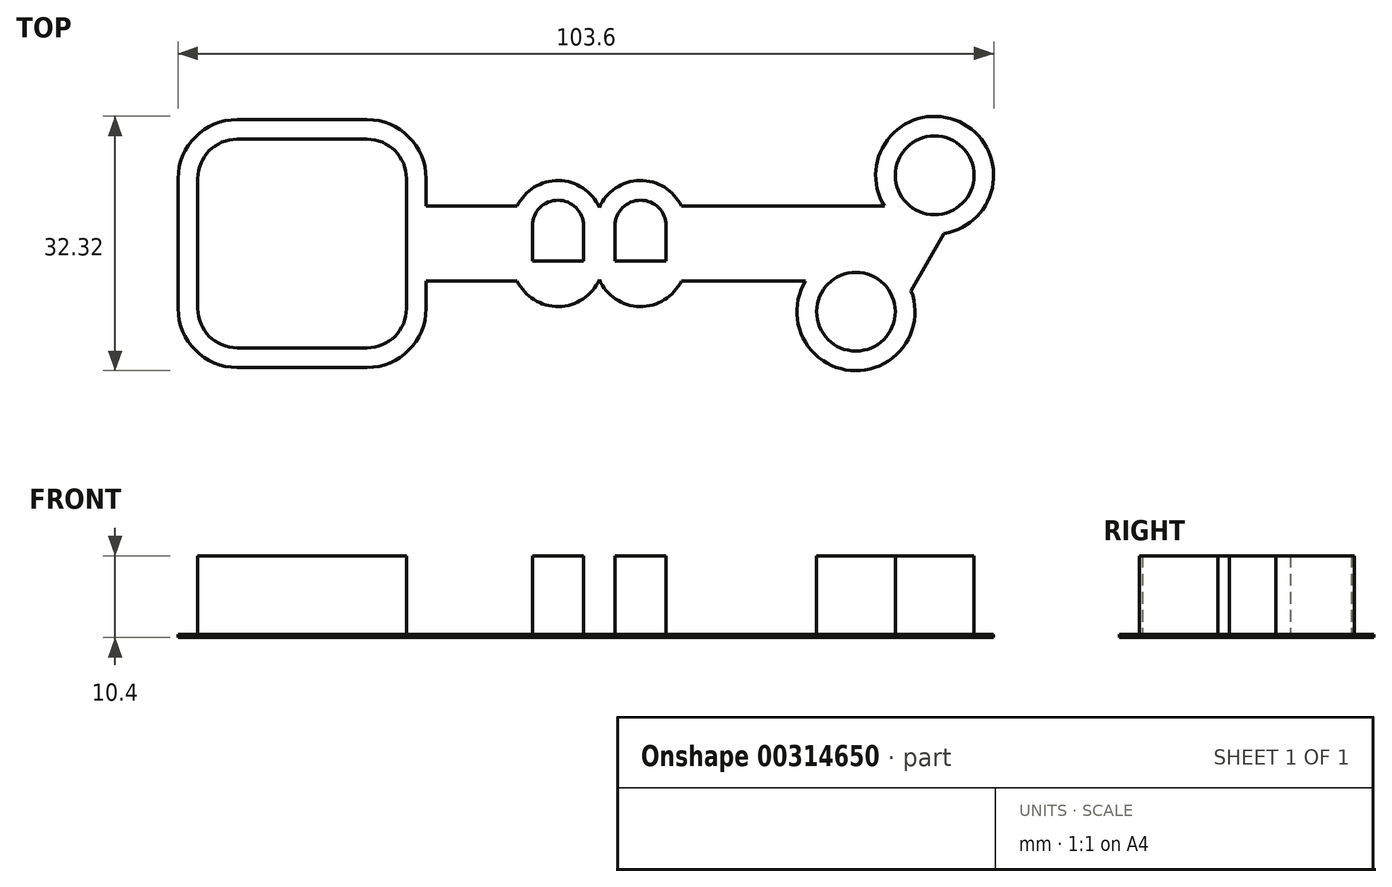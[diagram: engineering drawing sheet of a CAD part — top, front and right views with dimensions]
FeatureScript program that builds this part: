
annotation { "Feature Type Name" : "Feature", "Feature Type Description" : "" }
export const myFeature = defineFeature(function(context is Context, id is Id, definition is map)
    precondition{}
    {
        {
            var Q0;
            Q0=qCreatedBy(makeId("Top.planeOp"),FACE);
            var sketch = newSketch(context, id + "F0", { "sketchPlane" : qUnion([Q0])});
            skLineSegment(sketch, "E0.bottom", {"start": v(8.25, 13.25) * mm, "end": v(-8.25, 13.25) * mm});
            skLineSegment(sketch, "E0.top", {"start": v(8.25, -13.25) * mm, "end": v(-8.25, -13.25) * mm});
            skLineSegment(sketch, "E0.left", {"start": v(13.25, 8.25) * mm, "end": v(13.25, 2.25) * mm});
            skLineSegment(sketch, "E0.right", {"start": v(-13.25, 8.25) * mm, "end": v(-13.25, -8.25) * mm});
            skPoint(sketch, "E0.middle", {"position": v(0, 0) * mm});
            skPoint(sketch, "E1.visualSharp", {"position": v(-13.25, 13.25) * mm});
            skArc(sketch, "E1.filletArc", {"start": v(-8.25, 13.25) * mm, "mid": v(-11.79, 11.79) * mm, "end": v(-13.25, 8.25) * mm});
            skPoint(sketch, "E2.visualSharp", {"position": v(13.25, 13.25) * mm});
            skArc(sketch, "E2.filletArc", {"start": v(13.25, 8.25) * mm, "mid": v(11.79, 11.79) * mm, "end": v(8.25, 13.25) * mm});
            skPoint(sketch, "E3.visualSharp", {"position": v(13.25, -13.25) * mm});
            skArc(sketch, "E3.filletArc", {"start": v(8.25, -13.25) * mm, "mid": v(11.79, -11.79) * mm, "end": v(13.25, -8.25) * mm});
            skPoint(sketch, "E4.visualSharp", {"position": v(-13.25, -13.25) * mm});
            skArc(sketch, "E4.filletArc", {"start": v(-13.25, -8.25) * mm, "mid": v(-11.79, -11.79) * mm, "end": v(-8.25, -13.25) * mm});
            skCircle(sketch, "E5", {"center": v(0, 0) * mm, "radius": 4.5 * mm});
            skLineSegment(sketch, "E6", {"start": v(-4.5, 13.25) * mm, "end": v(-4.5, -13.25) * mm});
            skLineSegment(sketch, "E7", {"start": v(4.5, 13.25) * mm, "end": v(4.5, -13.25) * mm});
            skLineSegment(sketch, "E8", {"start": v(-13.25, 4.5) * mm, "end": v(13.25, 4.5) * mm});
            skLineSegment(sketch, "E9", {"start": v(-13.25, -4.5) * mm, "end": v(13.25, -4.5) * mm});
            skLineSegment(sketch, "E10", {"start": v(-129.37, 0) * mm, "end": v(144.98, 0) * mm, "construction": true});
            skPoint(sketch, "E10.startSnap0", {"position": v(-13.25, 0) * mm});
            skPoint(sketch, "E10.endSnap0", {"position": v(13.25, 0) * mm});
            skLineSegment(sketch, "E11", {"start": v(13.25, 2.25) * mm, "end": v(13.25, 2.25) * mm});
            skLineSegment(sketch, "E12.MirrorCS", {"start": v(13.25, -2.25) * mm, "end": v(29.25, -2.25) * mm});
            skLineSegment(sketch, "E13.bottom", {"start": v(29.25, 2.25) * mm, "end": v(35.75, 2.25) * mm});
            skLineSegment(sketch, "E13.top", {"start": v(29.25, -2.25) * mm, "end": v(35.75, -2.25) * mm});
            skLineSegment(sketch, "E13.left", {"start": v(29.25, 2.25) * mm, "end": v(29.25, -2.25) * mm});
            skLineSegment(sketch, "E13.right", {"start": v(35.75, 2.25) * mm, "end": v(35.75, -2.25) * mm});
            skLineSegment(sketch, "E14", {"start": v(37.75, 27.76) * mm, "end": v(37.75, -22.07) * mm, "construction": true});
            skLineSegment(sketch, "E15.MirrorCS", {"start": v(39.75, 2.25) * mm, "end": v(39.75, -2.25) * mm});
            skLineSegment(sketch, "E16.MirrorCS", {"start": v(46.25, -2.25) * mm, "end": v(39.75, -2.25) * mm});
            skLineSegment(sketch, "E17.MirrorCS", {"start": v(46.25, 2.25) * mm, "end": v(39.75, 2.25) * mm});
            skLineSegment(sketch, "E18.MirrorCS", {"start": v(46.25, 2.25) * mm, "end": v(46.25, -2.25) * mm});
            skLineSegment(sketch, "E19", {"start": v(35.75, 2.25) * mm, "end": v(39.75, 2.25) * mm});
            skLineSegment(sketch, "E20", {"start": v(35.75, -2.25) * mm, "end": v(39.75, -2.25) * mm});
            skArc(sketch, "E21", {"start": v(29.25, 2.25) * mm, "mid": v(32.5, 5.5) * mm, "end": v(35.75, 2.25) * mm});
            skArc(sketch, "E22.MirrorCS", {"start": v(46.25, 2.25) * mm, "mid": v(43, 5.5) * mm, "end": v(39.75, 2.25) * mm});
            skArc(sketch, "E23.MirrorCS", {"start": v(46.25, -2.25) * mm, "mid": v(43, -5.5) * mm, "end": v(39.75, -2.25) * mm});
            skArc(sketch, "E24.MirrorCS", {"start": v(29.25, -2.25) * mm, "mid": v(32.5, -5.5) * mm, "end": v(35.75, -2.25) * mm});
            skLineSegment(sketch, "E25", {"start": v(80.35, 8.66) * mm, "end": v(70.35, -8.66) * mm, "construction": true});
            skPoint(sketch, "E26", {"position": v(75.35, 0) * mm});
            skLineSegment(sketch, "E27", {"start": v(76.17, 5.92) * mm, "end": v(74.05, 2.25) * mm});
            skLineSegment(sketch, "E28.MirrorCS", {"start": v(80.06, 3.67) * mm, "end": v(74.53, -5.92) * mm});
            skPoint(sketch, "E29", {"position": v(72.75, 0) * mm});
            skLineSegment(sketch, "E30", {"start": v(46.25, 2.25) * mm, "end": v(74.05, 2.25) * mm});
            skLineSegment(sketch, "E31.MirrorCS", {"start": v(46.25, -2.25) * mm, "end": v(71.45, -2.25) * mm});
            skLineSegment(sketch, "E32", {"start": v(13.25, 2.25) * mm, "end": v(29.25, 2.25) * mm});
            skLineSegment(sketch, "E33", {"start": v(13.25, -2.25) * mm, "end": v(13.25, -8.25) * mm});
            skLineSegment(sketch, "E34", {"start": v(74.05, 2.25) * mm, "end": v(71.45, -2.25) * mm});
            skLineSegment(sketch, "E35", {"start": v(71.45, -2.25) * mm, "end": v(71.45, -2.25) * mm});
            skArc(sketch, "E36", {"start": v(70.63, -3.67) * mm, "mid": v(67.85, -13) * mm, "end": v(74.53, -5.92) * mm});
            skArc(sketch, "E37", {"start": v(74.53, -5.92) * mm, "mid": v(72.85, -4.33) * mm, "end": v(70.63, -3.67) * mm});
            skArc(sketch, "E38", {"start": v(76.17, 5.92) * mm, "mid": v(77.85, 4.33) * mm, "end": v(80.06, 3.67) * mm});
            skArc(sketch, "E39", {"start": v(80.06, 3.67) * mm, "mid": v(82.85, 13) * mm, "end": v(76.17, 5.92) * mm});
            skLineSegment(sketch, "E40", {"start": v(71.45, -2.25) * mm, "end": v(70.63, -3.67) * mm});
            skLineSegment(sketch, "E41", {"start": v(13.25, 2.25) * mm, "end": v(13.25, -2.25) * mm});
            skLineSegment(sketch, "E42.0", {"start": v(15.75, 8.25) * mm, "end": v(15.75, 4.75) * mm});
            skArc(sketch, "E42.1", {"start": v(15.75, 8.25) * mm, "mid": v(13.55, 13.55) * mm, "end": v(8.25, 15.75) * mm});
            skLineSegment(sketch, "E42.2", {"start": v(8.25, 15.75) * mm, "end": v(-8.25, 15.75) * mm});
            skArc(sketch, "E42.3", {"start": v(-8.25, 15.75) * mm, "mid": v(-13.55, 13.55) * mm, "end": v(-15.75, 8.25) * mm});
            skLineSegment(sketch, "E42.4", {"start": v(-15.75, 8.25) * mm, "end": v(-15.75, -8.25) * mm});
            skLineSegment(sketch, "E42.5", {"start": v(15.75, 4.75) * mm, "end": v(27.32, 4.75) * mm});
            skArc(sketch, "E42.6", {"start": v(-15.75, -8.25) * mm, "mid": v(-13.55, -13.55) * mm, "end": v(-8.25, -15.75) * mm});
            skLineSegment(sketch, "E42.7", {"start": v(8.25, -15.75) * mm, "end": v(-8.25, -15.75) * mm});
            skArc(sketch, "E42.8", {"start": v(8.25, -15.75) * mm, "mid": v(13.55, -13.55) * mm, "end": v(15.75, -8.25) * mm});
            skLineSegment(sketch, "E42.9", {"start": v(15.75, -4.75) * mm, "end": v(15.75, -8.25) * mm});
            skArc(sketch, "E42.10", {"start": v(81.56, 1.26) * mm, "mid": v(83.47, 15.48) * mm, "end": v(73.95, 4.75) * mm});
            skLineSegment(sketch, "E42.11", {"start": v(48.18, 4.75) * mm, "end": v(73.95, 4.75) * mm});
            skArc(sketch, "E42.12", {"start": v(48.18, 4.75) * mm, "mid": v(42.91, 8) * mm, "end": v(37.75, 4.6) * mm});
            skArc(sketch, "E42.13", {"start": v(27.32, 4.75) * mm, "mid": v(32.59, 8) * mm, "end": v(37.75, 4.6) * mm});
            skLineSegment(sketch, "E42.14", {"start": v(81.56, 1.26) * mm, "end": v(77.36, -6) * mm});
            skArc(sketch, "E42.15", {"start": v(63.95, -4.75) * mm, "mid": v(69.65, -16.13) * mm, "end": v(77.36, -6) * mm});
            skLineSegment(sketch, "E42.16", {"start": v(48.18, -4.75) * mm, "end": v(63.95, -4.75) * mm});
            skArc(sketch, "E42.17", {"start": v(48.18, -4.75) * mm, "mid": v(42.91, -8) * mm, "end": v(37.75, -4.6) * mm});
            skArc(sketch, "E42.18", {"start": v(27.32, -4.75) * mm, "mid": v(32.59, -8) * mm, "end": v(37.75, -4.6) * mm});
            skLineSegment(sketch, "E42.19", {"start": v(15.75, -4.75) * mm, "end": v(27.32, -4.75) * mm});
            skSolve(sketch);
        }
        {
            var Q0;
            {var subQ10=sQuery(id+"F0.wireOp",EDGE,"E1.filletArc");Q0=makeQuery(id+"F0.imprint","IMPRINT",FACE,{"disambiguationData":[TD([[makeQuery(id+"F0.imprint","IMPRINT",EDGE,{"derivedFrom":subQ10}),-1.0]])]});}
            var Q1;
            Q1=makeQuery(id+"F0.imprint","IMPRINT",FACE,{"disambiguationData":[TD([[makeQuery(id+"F0.imprint","IMPRINT",EDGE,{"derivedFrom":sQuery(id+"F0.wireOp",EDGE,"E13.right")}),1.0]])]});
            var Q2;
            {var subQ0=sQuery(id+"F0.wireOp",EDGE,"E8");var subQ1=sQuery(id+"F0.wireOp",EDGE,"E5");var subQ2=makeQuery(id+"F0.imprint","INTERSECT",VERTEX,{"derivedFrom":[subQ1,subQ0]});Q2=makeQuery(id+"F0.imprint","IMPRINT",FACE,{"disambiguationData":[TD([[makeQuery(id+"F0.imprint","IMPRINT",EDGE,{"disambiguationData":[TD([[subQ2,1.0]])],"derivedFrom":subQ1}),-1.0]])]});}
            var Q3;
            Q3=makeQuery(id+"F0.imprint","IMPRINT",FACE,{"disambiguationData":[TD([[makeQuery(id+"F0.imprint","IMPRINT",EDGE,{"derivedFrom":sQuery(id+"F0.wireOp",EDGE,"E12.MirrorCS")}),1.0]])]});
            var Q4;
            Q4=makeQuery(id+"F0.imprint","IMPRINT",FACE,{"disambiguationData":[TD([[makeQuery(id+"F0.imprint","IMPRINT",EDGE,{"derivedFrom":sQuery(id+"F0.wireOp",EDGE,"E18.MirrorCS")}),1.0]])]});
            var Q5;
            {var subQ5=sQuery(id+"F0.wireOp",EDGE,"E2.filletArc");Q5=makeQuery(id+"F0.imprint","IMPRINT",FACE,{"disambiguationData":[TD([[makeQuery(id+"F0.imprint","IMPRINT",EDGE,{"derivedFrom":subQ5}),1.0]])]});}
            var Q6;
            {var subQ2=sQuery(id+"F0.wireOp",EDGE,"E6");var subQ5=sQuery(id+"F0.wireOp",EDGE,"E0.bottom");var subQ8=makeQuery(id+"F0.imprint","INTERSECT",VERTEX,{"derivedFrom":[subQ5,subQ2]});Q6=makeQuery(id+"F0.imprint","IMPRINT",FACE,{"disambiguationData":[TD([[makeQuery(id+"F0.imprint","IMPRINT",EDGE,{"disambiguationData":[TD([[subQ8,1.0]])],"derivedFrom":subQ5}),1.0]])]});}
            var Q7;
            {var subQ0=sQuery(id+"F0.wireOp",EDGE,"E8");var subQ1=sQuery(id+"F0.wireOp",EDGE,"E5");var subQ2=makeQuery(id+"F0.imprint","INTERSECT",VERTEX,{"derivedFrom":[subQ1,subQ0]});Q7=makeQuery(id+"F0.imprint","IMPRINT",FACE,{"disambiguationData":[TD([[makeQuery(id+"F0.imprint","IMPRINT",EDGE,{"disambiguationData":[TD([[subQ2,-1.0]])],"derivedFrom":subQ1}),-1.0]])]});}
            var Q8;
            {var subQ5=sQuery(id+"F0.wireOp",EDGE,"E1.filletArc");Q8=makeQuery(id+"F0.imprint","IMPRINT",FACE,{"disambiguationData":[TD([[makeQuery(id+"F0.imprint","IMPRINT",EDGE,{"derivedFrom":subQ5}),1.0]])]});}
            var Q9;
            {var subQ0=sQuery(id+"F0.wireOp",EDGE,"E6");var subQ1=sQuery(id+"F0.wireOp",EDGE,"E5");var subQ2=makeQuery(id+"F0.imprint","INTERSECT",VERTEX,{"derivedFrom":[subQ1,subQ0]});Q9=makeQuery(id+"F0.imprint","IMPRINT",FACE,{"disambiguationData":[TD([[makeQuery(id+"F0.imprint","IMPRINT",EDGE,{"disambiguationData":[TD([[subQ2,-1.0]])],"derivedFrom":subQ1}),-1.0]])]});}
            var Q10;
            {var subQ0=sQuery(id+"F0.wireOp",EDGE,"E8");var subQ1=sQuery(id+"F0.wireOp",EDGE,"E0.right");var subQ2=makeQuery(id+"F0.imprint","INTERSECT",VERTEX,{"derivedFrom":[subQ1,subQ0]});Q10=makeQuery(id+"F0.imprint","IMPRINT",FACE,{"disambiguationData":[TD([[makeQuery(id+"F0.imprint","IMPRINT",EDGE,{"disambiguationData":[TD([[subQ2,-1.0]])],"derivedFrom":subQ1}),1.0]])]});}
            var Q11;
            Q11=makeQuery(id+"F0.imprint","IMPRINT",FACE,{"disambiguationData":[TD([[makeQuery(id+"F0.imprint","IMPRINT",EDGE,{"derivedFrom":sQuery(id+"F0.wireOp",EDGE,"E27")}),1.0]])]});
            var Q12;
            {var subQ5=sQuery(id+"F0.wireOp",EDGE,"E3.filletArc");Q12=makeQuery(id+"F0.imprint","IMPRINT",FACE,{"disambiguationData":[TD([[makeQuery(id+"F0.imprint","IMPRINT",EDGE,{"derivedFrom":subQ5}),1.0]])]});}
            var Q13;
            {var subQ1=sQuery(id+"F0.wireOp",EDGE,"E0.top");var subQ5=sQuery(id+"F0.wireOp",EDGE,"E6");var subQ6=makeQuery(id+"F0.imprint","INTERSECT",VERTEX,{"derivedFrom":[subQ1,subQ5]});Q13=makeQuery(id+"F0.imprint","IMPRINT",FACE,{"disambiguationData":[TD([[makeQuery(id+"F0.imprint","IMPRINT",EDGE,{"disambiguationData":[TD([[subQ6,1.0]])],"derivedFrom":subQ1}),-1.0]])]});}
            var Q14;
            {var subQ5=sQuery(id+"F0.wireOp",EDGE,"E4.filletArc");Q14=makeQuery(id+"F0.imprint","IMPRINT",FACE,{"disambiguationData":[TD([[makeQuery(id+"F0.imprint","IMPRINT",EDGE,{"derivedFrom":subQ5}),1.0]])]});}
            var Q15;
            {var subQ0=sQuery(id+"F0.wireOp",EDGE,"E5");var subQ1=makeQuery(id+"F0.imprint","INTERSECT",VERTEX,{"derivedFrom":[subQ0,sQuery(id+"F0.wireOp",EDGE,"E8")]});Q15=makeQuery(id+"F0.imprint","IMPRINT",FACE,{"disambiguationData":[TD([[makeQuery(id+"F0.imprint","IMPRINT",EDGE,{"disambiguationData":[TD([[subQ1,1.0]])],"derivedFrom":subQ0}),1.0]])]});}
            var Q16;
            Q16=makeQuery(id+"F0.imprint","IMPRINT",FACE,{"disambiguationData":[TD([[makeQuery(id+"F0.imprint","IMPRINT",EDGE,{"derivedFrom":sQuery(id+"F0.wireOp",EDGE,"E13.bottom")}),1.0]])]});
            var Q17;
            {var subQ0=sQuery(id+"F0.wireOp",EDGE,"E7");var subQ1=sQuery(id+"F0.wireOp",EDGE,"E5");var subQ2=makeQuery(id+"F0.imprint","INTERSECT",VERTEX,{"derivedFrom":[subQ1,subQ0]});Q17=makeQuery(id+"F0.imprint","IMPRINT",FACE,{"disambiguationData":[TD([[makeQuery(id+"F0.imprint","IMPRINT",EDGE,{"disambiguationData":[TD([[subQ2,1.0]])],"derivedFrom":subQ1}),-1.0]])]});}
            var Q18;
            Q18=makeQuery(id+"F0.imprint","IMPRINT",FACE,{"disambiguationData":[TD([[makeQuery(id+"F0.imprint","IMPRINT",EDGE,{"derivedFrom":sQuery(id+"F0.wireOp",EDGE,"E16.MirrorCS")}),1.0]])]});
            var Q19;
            Q19=makeQuery(id+"F0.imprint","IMPRINT",FACE,{"disambiguationData":[TD([[makeQuery(id+"F0.imprint","IMPRINT",EDGE,{"derivedFrom":sQuery(id+"F0.wireOp",EDGE,"E17.MirrorCS")}),-1.0]])]});
            var Q20;
            Q20=makeQuery(id+"F0.imprint","IMPRINT",FACE,{"disambiguationData":[TD([[makeQuery(id+"F0.imprint","IMPRINT",EDGE,{"derivedFrom":sQuery(id+"F0.wireOp",EDGE,"E13.top")}),-1.0]])]});
            var Q21;
            Q21=makeQuery(id+"F0.imprint","IMPRINT",FACE,{"disambiguationData":[TD([[makeQuery(id+"F0.imprint","IMPRINT",EDGE,{"derivedFrom":sQuery(id+"F0.wireOp",EDGE,"E36")}),1.0]])]});
            var Q22;
            Q22=makeQuery(id+"F0.imprint","IMPRINT",FACE,{"disambiguationData":[TD([[makeQuery(id+"F0.imprint","IMPRINT",EDGE,{"derivedFrom":sQuery(id+"F0.wireOp",EDGE,"E38")}),1.0]])]});
            var Q23;
            {var subQ5=sQuery(id+"F0.wireOp",EDGE,"E41");Q23=makeQuery(id+"F0.imprint","IMPRINT",FACE,{"disambiguationData":[TD([[makeQuery(id+"F0.imprint","IMPRINT",EDGE,{"derivedFrom":subQ5}),-1.0]])]});}
            var Q24;
            Q24=makeQuery(id+"F0.imprint","IMPRINT",FACE,{"disambiguationData":[TD([[makeQuery(id+"F0.imprint","IMPRINT",EDGE,{"derivedFrom":sQuery(id+"F0.wireOp",EDGE,"E13.bottom")}),-1.0]])]});
            var Q25;
            Q25=makeQuery(id+"F0.imprint","IMPRINT",FACE,{"disambiguationData":[TD([[makeQuery(id+"F0.imprint","IMPRINT",EDGE,{"derivedFrom":sQuery(id+"F0.wireOp",EDGE,"E15.MirrorCS")}),1.0]])]});
            extrude(context, id + "F1", {"entities" : qUnion([Q0, Q1, Q2, Q3, Q4, Q5, Q6, Q7, Q8, Q9, Q10, Q11, Q12, Q13, Q14, Q15, Q16, Q17, Q18, Q19, Q20, Q21, Q22, Q23, Q24, Q25]), "depth" : 0.4 * mm});
        }
        {
            var Q0;
            Q0=makeQuery(id+"F1.opExtrude","CAP_FACE",FACE,{"disambiguationData":[OSD([sQuery(id+"F0.wireOp",EDGE,"E42.0"),sQuery(id+"F0.wireOp",EDGE,"E42.1"),sQuery(id+"F0.wireOp",EDGE,"E42.2"),sQuery(id+"F0.wireOp",EDGE,"E42.3"),sQuery(id+"F0.wireOp",EDGE,"E42.4"),sQuery(id+"F0.wireOp",EDGE,"E42.5"),sQuery(id+"F0.wireOp",EDGE,"E42.6"),sQuery(id+"F0.wireOp",EDGE,"E42.7"),sQuery(id+"F0.wireOp",EDGE,"E42.8"),sQuery(id+"F0.wireOp",EDGE,"E42.9"),sQuery(id+"F0.wireOp",EDGE,"E42.10"),sQuery(id+"F0.wireOp",EDGE,"E42.11"),sQuery(id+"F0.wireOp",EDGE,"E42.12"),sQuery(id+"F0.wireOp",EDGE,"E42.13"),sQuery(id+"F0.wireOp",EDGE,"E42.14"),sQuery(id+"F0.wireOp",EDGE,"E42.15"),sQuery(id+"F0.wireOp",EDGE,"E42.16"),sQuery(id+"F0.wireOp",EDGE,"E42.17"),sQuery(id+"F0.wireOp",EDGE,"E42.18"),sQuery(id+"F0.wireOp",EDGE,"E42.19")])],"isStart":false});
            var sketch = newSketch(context, id + "F2", { "sketchPlane" : qUnion([Q0])});
            skLineSegment(sketch, "E43.0", {"start": v(8.25, 13.25) * mm, "end": v(-8.25, 13.25) * mm});
            skLineSegment(sketch, "E43.1", {"start": v(8.25, -13.25) * mm, "end": v(-8.25, -13.25) * mm});
            skLineSegment(sketch, "E43.2", {"start": v(13.25, 8.25) * mm, "end": v(13.25, 2.25) * mm});
            skLineSegment(sketch, "E43.3", {"start": v(-13.25, 8.25) * mm, "end": v(-13.25, -8.25) * mm});
            skPoint(sketch, "E43.4", {"position": v(0, 0) * mm});
            skPoint(sketch, "E43.5", {"position": v(-13.25, 13.25) * mm});
            skArc(sketch, "E43.6", {"start": v(-8.25, 13.25) * mm, "mid": v(-11.79, 11.79) * mm, "end": v(-13.25, 8.25) * mm});
            skPoint(sketch, "E43.7", {"position": v(13.25, 13.25) * mm});
            skArc(sketch, "E43.8", {"start": v(13.25, 8.25) * mm, "mid": v(11.79, 11.79) * mm, "end": v(8.25, 13.25) * mm});
            skPoint(sketch, "E43.9", {"position": v(13.25, -13.25) * mm});
            skArc(sketch, "E43.10", {"start": v(8.25, -13.25) * mm, "mid": v(11.79, -11.79) * mm, "end": v(13.25, -8.25) * mm});
            skPoint(sketch, "E43.11", {"position": v(-13.25, -13.25) * mm});
            skArc(sketch, "E43.12", {"start": v(-13.25, -8.25) * mm, "mid": v(-11.79, -11.79) * mm, "end": v(-8.25, -13.25) * mm});
            skCircle(sketch, "E43.13", {"center": v(0, 0) * mm, "radius": 4.5 * mm});
            skLineSegment(sketch, "E43.14", {"start": v(-4.5, 13.25) * mm, "end": v(-4.5, -13.25) * mm});
            skLineSegment(sketch, "E43.15", {"start": v(4.5, 13.25) * mm, "end": v(4.5, -13.25) * mm});
            skLineSegment(sketch, "E43.16", {"start": v(-13.25, 4.5) * mm, "end": v(13.25, 4.5) * mm});
            skLineSegment(sketch, "E43.17", {"start": v(-13.25, -4.5) * mm, "end": v(13.25, -4.5) * mm});
            skPoint(sketch, "E43.19", {"position": v(-13.25, 0) * mm});
            skPoint(sketch, "E43.20", {"position": v(13.25, 0) * mm});
            skPoint(sketch, "E43.21", {"position": v(13.25, 2.25) * mm});
            skLineSegment(sketch, "E43.22", {"start": v(13.25, -2.25) * mm, "end": v(29.25, -2.25) * mm});
            skLineSegment(sketch, "E43.23", {"start": v(29.25, 2.25) * mm, "end": v(35.75, 2.25) * mm});
            skLineSegment(sketch, "E43.24", {"start": v(29.25, -2.25) * mm, "end": v(35.75, -2.25) * mm});
            skLineSegment(sketch, "E43.25", {"start": v(29.25, 2.25) * mm, "end": v(29.25, -2.25) * mm});
            skLineSegment(sketch, "E43.26", {"start": v(35.75, 2.25) * mm, "end": v(35.75, -2.25) * mm});
            skLineSegment(sketch, "E43.28", {"start": v(39.75, 2.25) * mm, "end": v(39.75, -2.25) * mm});
            skLineSegment(sketch, "E43.29", {"start": v(46.25, -2.25) * mm, "end": v(39.75, -2.25) * mm});
            skLineSegment(sketch, "E43.30", {"start": v(46.25, 2.25) * mm, "end": v(39.75, 2.25) * mm});
            skLineSegment(sketch, "E43.31", {"start": v(46.25, 2.25) * mm, "end": v(46.25, -2.25) * mm});
            skLineSegment(sketch, "E43.32", {"start": v(35.75, 2.25) * mm, "end": v(39.75, 2.25) * mm});
            skLineSegment(sketch, "E43.33", {"start": v(35.75, -2.25) * mm, "end": v(39.75, -2.25) * mm});
            skArc(sketch, "E43.34", {"start": v(29.25, 2.25) * mm, "mid": v(32.5, 5.5) * mm, "end": v(35.75, 2.25) * mm});
            skArc(sketch, "E43.35", {"start": v(46.25, 2.25) * mm, "mid": v(43, 5.5) * mm, "end": v(39.75, 2.25) * mm});
            skLineSegment(sketch, "E43.36", {"start": v(46.25, -2.25) * mm, "end": v(39.75, -2.25) * mm});
            skArc(sketch, "E43.37", {"start": v(46.25, -2.25) * mm, "mid": v(43, -5.5) * mm, "end": v(39.75, -2.25) * mm});
            skLineSegment(sketch, "E43.38", {"start": v(35.75, -2.25) * mm, "end": v(39.75, -2.25) * mm});
            skLineSegment(sketch, "E43.39", {"start": v(29.25, -2.25) * mm, "end": v(35.75, -2.25) * mm});
            skArc(sketch, "E43.40", {"start": v(29.25, -2.25) * mm, "mid": v(32.5, -5.5) * mm, "end": v(35.75, -2.25) * mm});
            skLineSegment(sketch, "E43.41", {"start": v(80.35, 8.66) * mm, "end": v(70.35, -8.66) * mm});
            skPoint(sketch, "E43.42", {"position": v(75.35, 0) * mm});
            skLineSegment(sketch, "E43.43", {"start": v(76.17, 5.92) * mm, "end": v(74.05, 2.25) * mm});
            skLineSegment(sketch, "E43.44", {"start": v(80.06, 3.67) * mm, "end": v(74.53, -5.92) * mm});
            skPoint(sketch, "E43.45", {"position": v(72.75, 0) * mm});
            skLineSegment(sketch, "E43.46", {"start": v(46.25, 2.25) * mm, "end": v(74.05, 2.25) * mm});
            skLineSegment(sketch, "E43.47", {"start": v(46.25, -2.25) * mm, "end": v(71.45, -2.25) * mm});
            skLineSegment(sketch, "E43.48", {"start": v(13.25, 2.25) * mm, "end": v(29.25, 2.25) * mm});
            skLineSegment(sketch, "E43.49", {"start": v(13.25, -2.25) * mm, "end": v(13.25, -8.25) * mm});
            skLineSegment(sketch, "E43.50", {"start": v(74.05, 2.25) * mm, "end": v(71.45, -2.25) * mm});
            skPoint(sketch, "E43.51", {"position": v(71.45, -2.25) * mm});
            skArc(sketch, "E43.52", {"start": v(70.63, -3.67) * mm, "mid": v(67.85, -13) * mm, "end": v(74.53, -5.92) * mm});
            skArc(sketch, "E43.53", {"start": v(74.53, -5.92) * mm, "mid": v(72.85, -4.33) * mm, "end": v(70.63, -3.67) * mm});
            skArc(sketch, "E43.54", {"start": v(76.17, 5.92) * mm, "mid": v(77.85, 4.33) * mm, "end": v(80.06, 3.67) * mm});
            skArc(sketch, "E43.55", {"start": v(80.06, 3.67) * mm, "mid": v(82.85, 13) * mm, "end": v(76.17, 5.92) * mm});
            skLineSegment(sketch, "E43.56", {"start": v(71.45, -2.25) * mm, "end": v(70.63, -3.67) * mm});
            skLineSegment(sketch, "E43.57", {"start": v(13.25, 2.25) * mm, "end": v(13.25, -2.25) * mm});
            skLineSegment(sketch, "E43.58", {"start": v(15.75, 8.25) * mm, "end": v(15.75, 4.75) * mm});
            skArc(sketch, "E43.59", {"start": v(15.75, 8.25) * mm, "mid": v(13.55, 13.55) * mm, "end": v(8.25, 15.75) * mm});
            skLineSegment(sketch, "E43.60", {"start": v(8.25, 15.75) * mm, "end": v(-8.25, 15.75) * mm});
            skArc(sketch, "E43.61", {"start": v(-8.25, 15.75) * mm, "mid": v(-13.55, 13.55) * mm, "end": v(-15.75, 8.25) * mm});
            skLineSegment(sketch, "E43.62", {"start": v(-15.75, 8.25) * mm, "end": v(-15.75, -8.25) * mm});
            skLineSegment(sketch, "E43.63", {"start": v(15.75, 4.75) * mm, "end": v(27.32, 4.75) * mm});
            skArc(sketch, "E43.64", {"start": v(-15.75, -8.25) * mm, "mid": v(-13.55, -13.55) * mm, "end": v(-8.25, -15.75) * mm});
            skLineSegment(sketch, "E43.65", {"start": v(8.25, -15.75) * mm, "end": v(-8.25, -15.75) * mm});
            skArc(sketch, "E43.66", {"start": v(8.25, -15.75) * mm, "mid": v(13.55, -13.55) * mm, "end": v(15.75, -8.25) * mm});
            skLineSegment(sketch, "E43.67", {"start": v(15.75, -4.75) * mm, "end": v(15.75, -8.25) * mm});
            skArc(sketch, "E43.68", {"start": v(81.56, 1.26) * mm, "mid": v(83.47, 15.48) * mm, "end": v(73.95, 4.75) * mm});
            skLineSegment(sketch, "E43.69", {"start": v(48.18, 4.75) * mm, "end": v(73.95, 4.75) * mm});
            skArc(sketch, "E43.70", {"start": v(48.18, 4.75) * mm, "mid": v(42.91, 8) * mm, "end": v(37.75, 4.6) * mm});
            skArc(sketch, "E43.71", {"start": v(27.32, 4.75) * mm, "mid": v(32.59, 8) * mm, "end": v(37.75, 4.6) * mm});
            skLineSegment(sketch, "E43.72", {"start": v(81.56, 1.26) * mm, "end": v(77.36, -6) * mm});
            skArc(sketch, "E43.73", {"start": v(63.95, -4.75) * mm, "mid": v(69.65, -16.13) * mm, "end": v(77.36, -6) * mm});
            skLineSegment(sketch, "E43.74", {"start": v(48.18, -4.75) * mm, "end": v(63.95, -4.75) * mm});
            skArc(sketch, "E43.75", {"start": v(48.18, -4.75) * mm, "mid": v(42.91, -8) * mm, "end": v(37.75, -4.6) * mm});
            skArc(sketch, "E43.76", {"start": v(27.32, -4.75) * mm, "mid": v(32.59, -8) * mm, "end": v(37.75, -4.6) * mm});
            skLineSegment(sketch, "E43.77", {"start": v(15.75, -4.75) * mm, "end": v(27.32, -4.75) * mm});
            skSolve(sketch);
        }
        {
            var Q0;
            {var subQ0=sQuery(id+"F2.wireOp",EDGE,"E43.15");var subQ1=sQuery(id+"F2.wireOp",EDGE,"E43.13");var subQ2=makeQuery(id+"F2.imprint","INTERSECT",VERTEX,{"derivedFrom":[subQ1,subQ0]});Q0=makeQuery(id+"F2.imprint","IMPRINT",FACE,{"disambiguationData":[TD([[makeQuery(id+"F2.imprint","IMPRINT",EDGE,{"disambiguationData":[TD([[subQ2,1.0]])],"derivedFrom":subQ1}),-1.0]])]});}
            var Q1;
            {var subQ0=sQuery(id+"F2.wireOp",EDGE,"E43.13");var subQ1=makeQuery(id+"F2.imprint","INTERSECT",VERTEX,{"derivedFrom":[subQ0,sQuery(id+"F2.wireOp",EDGE,"E43.16")]});Q1=makeQuery(id+"F2.imprint","IMPRINT",FACE,{"disambiguationData":[TD([[makeQuery(id+"F2.imprint","IMPRINT",EDGE,{"disambiguationData":[TD([[subQ1,1.0]])],"derivedFrom":subQ0}),1.0]])]});}
            var Q2;
            {var subQ0=sQuery(id+"F2.wireOp",EDGE,"E43.16");var subQ1=sQuery(id+"F2.wireOp",EDGE,"E43.13");var subQ2=makeQuery(id+"F2.imprint","INTERSECT",VERTEX,{"derivedFrom":[subQ1,subQ0]});Q2=makeQuery(id+"F2.imprint","IMPRINT",FACE,{"disambiguationData":[TD([[makeQuery(id+"F2.imprint","IMPRINT",EDGE,{"disambiguationData":[TD([[subQ2,1.0]])],"derivedFrom":subQ1}),-1.0]])]});}
            var Q3;
            {var subQ0=sQuery(id+"F2.wireOp",EDGE,"E43.16");var subQ1=sQuery(id+"F2.wireOp",EDGE,"E43.13");var subQ2=makeQuery(id+"F2.imprint","INTERSECT",VERTEX,{"derivedFrom":[subQ1,subQ0]});Q3=makeQuery(id+"F2.imprint","IMPRINT",FACE,{"disambiguationData":[TD([[makeQuery(id+"F2.imprint","IMPRINT",EDGE,{"disambiguationData":[TD([[subQ2,-1.0]])],"derivedFrom":subQ1}),-1.0]])]});}
            var Q4;
            {var subQ0=sQuery(id+"F2.wireOp",EDGE,"E43.14");var subQ1=sQuery(id+"F2.wireOp",EDGE,"E43.13");var subQ2=makeQuery(id+"F2.imprint","INTERSECT",VERTEX,{"derivedFrom":[subQ1,subQ0]});Q4=makeQuery(id+"F2.imprint","IMPRINT",FACE,{"disambiguationData":[TD([[makeQuery(id+"F2.imprint","IMPRINT",EDGE,{"disambiguationData":[TD([[subQ2,-1.0]])],"derivedFrom":subQ1}),-1.0]])]});}
            var Q5;
            {var subQ8=sQuery(id+"F2.wireOp",EDGE,"E43.57");Q5=makeQuery(id+"F2.imprint","IMPRINT",FACE,{"disambiguationData":[TD([[makeQuery(id+"F2.imprint","IMPRINT",EDGE,{"derivedFrom":subQ8}),-1.0]])]});}
            var Q6;
            {var subQ5=sQuery(id+"F2.wireOp",EDGE,"E43.6");Q6=makeQuery(id+"F2.imprint","IMPRINT",FACE,{"disambiguationData":[TD([[makeQuery(id+"F2.imprint","IMPRINT",EDGE,{"derivedFrom":subQ5}),1.0]])]});}
            var Q7;
            {var subQ0=sQuery(id+"F2.wireOp",EDGE,"E43.16");var subQ1=sQuery(id+"F2.wireOp",EDGE,"E43.3");var subQ2=makeQuery(id+"F2.imprint","INTERSECT",VERTEX,{"derivedFrom":[subQ1,subQ0]});Q7=makeQuery(id+"F2.imprint","IMPRINT",FACE,{"disambiguationData":[TD([[makeQuery(id+"F2.imprint","IMPRINT",EDGE,{"disambiguationData":[TD([[subQ2,-1.0]])],"derivedFrom":subQ1}),1.0]])]});}
            var Q8;
            {var subQ5=sQuery(id+"F2.wireOp",EDGE,"E43.8");Q8=makeQuery(id+"F2.imprint","IMPRINT",FACE,{"disambiguationData":[TD([[makeQuery(id+"F2.imprint","IMPRINT",EDGE,{"derivedFrom":subQ5}),1.0]])]});}
            var Q9;
            {var subQ2=sQuery(id+"F2.wireOp",EDGE,"E43.14");var subQ5=sQuery(id+"F2.wireOp",EDGE,"E43.0");var subQ8=makeQuery(id+"F2.imprint","INTERSECT",VERTEX,{"derivedFrom":[subQ5,subQ2]});Q9=makeQuery(id+"F2.imprint","IMPRINT",FACE,{"disambiguationData":[TD([[makeQuery(id+"F2.imprint","IMPRINT",EDGE,{"disambiguationData":[TD([[subQ8,1.0]])],"derivedFrom":subQ5}),1.0]])]});}
            var Q10;
            {var subQ1=sQuery(id+"F2.wireOp",EDGE,"E43.1");var subQ5=sQuery(id+"F2.wireOp",EDGE,"E43.14");var subQ6=makeQuery(id+"F2.imprint","INTERSECT",VERTEX,{"derivedFrom":[subQ1,subQ5]});Q10=makeQuery(id+"F2.imprint","IMPRINT",FACE,{"disambiguationData":[TD([[makeQuery(id+"F2.imprint","IMPRINT",EDGE,{"disambiguationData":[TD([[subQ6,1.0]])],"derivedFrom":subQ1}),-1.0]])]});}
            var Q11;
            {var subQ5=sQuery(id+"F2.wireOp",EDGE,"E43.12");Q11=makeQuery(id+"F2.imprint","IMPRINT",FACE,{"disambiguationData":[TD([[makeQuery(id+"F2.imprint","IMPRINT",EDGE,{"derivedFrom":subQ5}),1.0]])]});}
            var Q12;
            {var subQ7=sQuery(id+"F2.wireOp",EDGE,"E43.10");Q12=makeQuery(id+"F2.imprint","IMPRINT",FACE,{"disambiguationData":[TD([[makeQuery(id+"F2.imprint","IMPRINT",EDGE,{"derivedFrom":subQ7}),1.0]])]});}
            var Q13;
            Q13=makeQuery(id+"F2.imprint","IMPRINT",FACE,{"disambiguationData":[TD([[makeQuery(id+"F2.imprint","IMPRINT",EDGE,{"derivedFrom":sQuery(id+"F2.wireOp",EDGE,"E43.23")}),-1.0]])]});
            var Q14;
            Q14=makeQuery(id+"F2.imprint","IMPRINT",FACE,{"disambiguationData":[TD([[makeQuery(id+"F2.imprint","IMPRINT",EDGE,{"derivedFrom":sQuery(id+"F2.wireOp",EDGE,"E43.23")}),1.0]])]});
            var Q15;
            Q15=makeQuery(id+"F2.imprint","IMPRINT",FACE,{"disambiguationData":[TD([[makeQuery(id+"F2.imprint","IMPRINT",EDGE,{"derivedFrom":sQuery(id+"F2.wireOp",EDGE,"E43.39")}),-1.0]])]});
            var Q16;
            Q16=makeQuery(id+"F2.imprint","IMPRINT",FACE,{"disambiguationData":[TD([[makeQuery(id+"F2.imprint","IMPRINT",EDGE,{"derivedFrom":sQuery(id+"F2.wireOp",EDGE,"E43.36")}),1.0]])]});
            var Q17;
            Q17=makeQuery(id+"F2.imprint","IMPRINT",FACE,{"disambiguationData":[TD([[makeQuery(id+"F2.imprint","IMPRINT",EDGE,{"derivedFrom":sQuery(id+"F2.wireOp",EDGE,"E43.28")}),1.0]])]});
            var Q18;
            Q18=makeQuery(id+"F2.imprint","IMPRINT",FACE,{"disambiguationData":[TD([[makeQuery(id+"F2.imprint","IMPRINT",EDGE,{"derivedFrom":sQuery(id+"F2.wireOp",EDGE,"E43.30")}),-1.0]])]});
            var Q19;
            {var subQ0=sQuery(id+"F2.wireOp",EDGE,"E43.52");Q19=makeQuery(id+"F2.imprint","IMPRINT",FACE,{"disambiguationData":[TD([[makeQuery(id+"F2.imprint","IMPRINT",EDGE,{"derivedFrom":subQ0}),1.0]])]});}
            var Q20;
            {var subQ0=sQuery(id+"F2.wireOp",EDGE,"E43.55");Q20=makeQuery(id+"F2.imprint","IMPRINT",FACE,{"disambiguationData":[TD([[makeQuery(id+"F2.imprint","IMPRINT",EDGE,{"derivedFrom":subQ0}),1.0]])]});}
            extrude(context, id + "F3", {"entities" : qUnion([Q0, Q1, Q2, Q3, Q4, Q5, Q6, Q7, Q8, Q9, Q10, Q11, Q12, Q13, Q14, Q15, Q16, Q17, Q18, Q19, Q20]), "operationType" : NewBodyOperationType.ADD, "depth" : 10 * mm});
        }
    });
